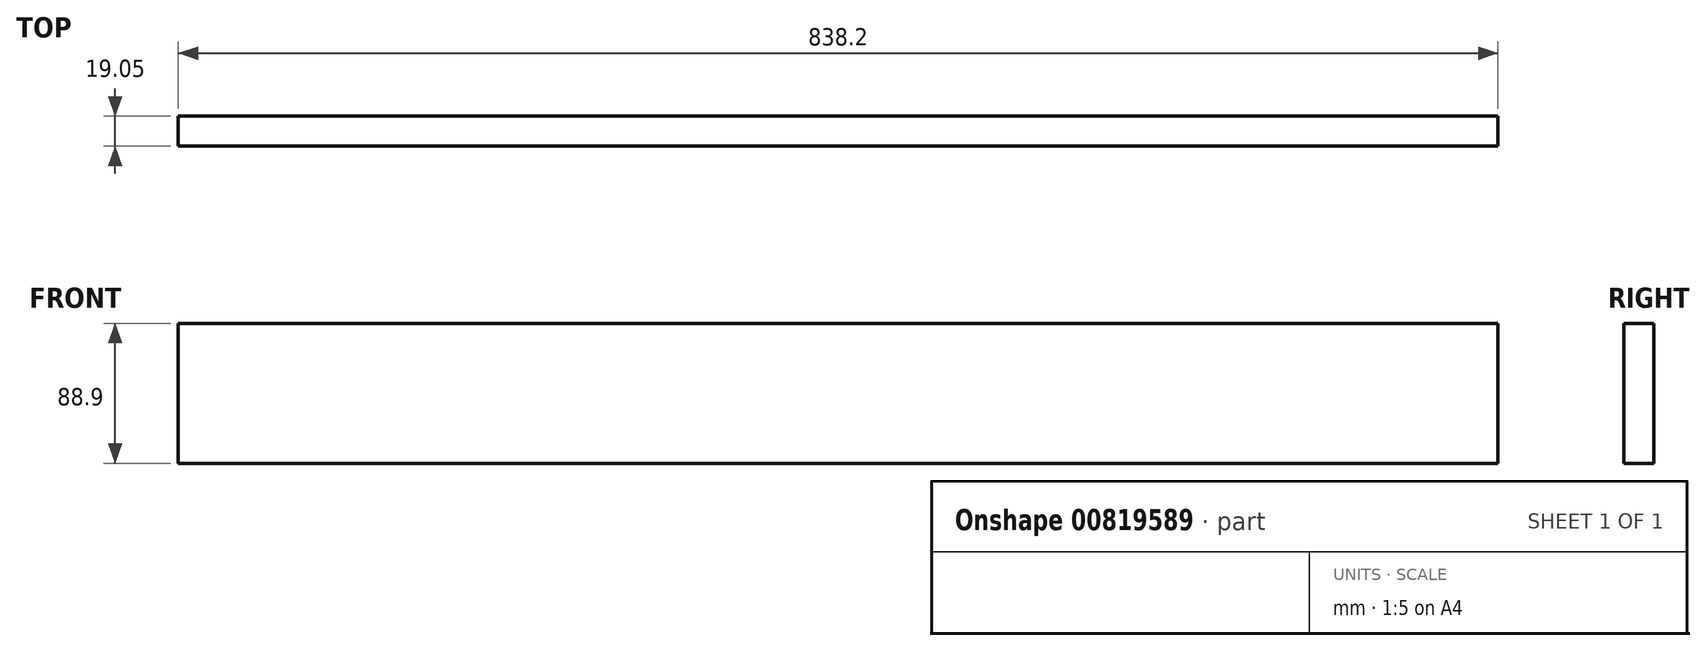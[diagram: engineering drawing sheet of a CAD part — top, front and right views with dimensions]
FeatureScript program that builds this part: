
annotation { "Feature Type Name" : "Feature", "Feature Type Description" : "" }
export const myFeature = defineFeature(function(context is Context, id is Id, definition is map)
    precondition{}
    {
        {
            var Q0;
            Q0=qCreatedBy(makeId("Front.planeOp"),FACE);
            var sketch = newSketch(context, id + "F0", { "sketchPlane" : qUnion([Q0])});
            skLineSegment(sketch, "E0.bottom", {"start": v(-417.46, 51.27) * mm, "end": v(420.74, 51.27) * mm});
            skLineSegment(sketch, "E0.top", {"start": v(-417.46, -37.63) * mm, "end": v(420.74, -37.63) * mm});
            skLineSegment(sketch, "E0.left", {"start": v(-417.46, 51.27) * mm, "end": v(-417.46, -37.63) * mm});
            skLineSegment(sketch, "E0.right", {"start": v(420.74, 51.27) * mm, "end": v(420.74, -37.63) * mm});
            skSolve(sketch);
        }
        {
            var Q0;
            Q0=makeQuery(id+"F0.imprint","IMPRINT",FACE,{"disambiguationData":[TD([[makeQuery(id+"F0.imprint","IMPRINT",EDGE,{"derivedFrom":sQuery(id+"F0.wireOp",EDGE,"E0.bottom")}),-1.0]])]});
            extrude(context, id + "F1", {"entities" : qUnion([Q0]), "depth" : 19.05 * mm, "offsetDistance" : 25.4 * mm});
        }
    });
